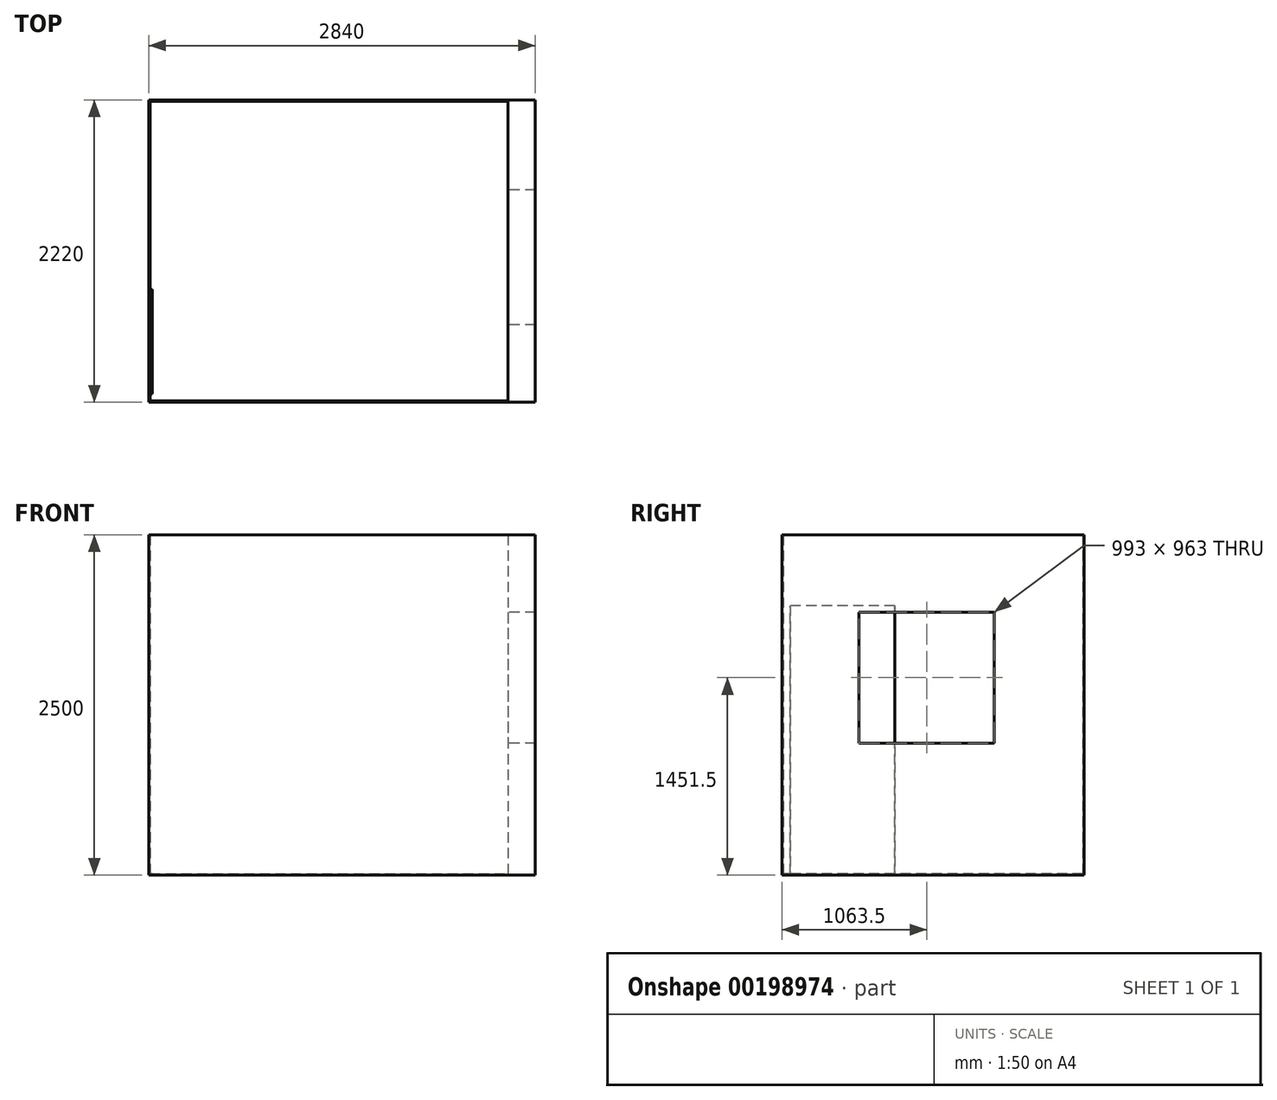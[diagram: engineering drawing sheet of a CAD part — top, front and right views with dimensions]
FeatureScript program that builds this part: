
annotation { "Feature Type Name" : "Feature", "Feature Type Description" : "" }
export const myFeature = defineFeature(function(context is Context, id is Id, definition is map)
    precondition{}
    {
        {
            var Q0;
            Q0=qCreatedBy(makeId("Top.planeOp"),FACE);
            var sketch = newSketch(context, id + "F0", { "sketchPlane" : qUnion([Q0])});
            skLineSegment(sketch, "E0.bottom", {"start": v(-2487.76, 778.4) * mm, "end": v(352.24, 778.4) * mm});
            skLineSegment(sketch, "E0.top", {"start": v(-2487.76, -1441.6) * mm, "end": v(352.24, -1441.6) * mm});
            skLineSegment(sketch, "E0.left", {"start": v(-2487.76, 778.4) * mm, "end": v(-2487.76, -1441.6) * mm});
            skLineSegment(sketch, "E0.right", {"start": v(352.24, 778.4) * mm, "end": v(352.24, -1441.6) * mm});
            skSolve(sketch);
        }
        {
            var Q0;
            Q0=makeQuery(id+"F0.imprint","IMPRINT",FACE,{"disambiguationData":[TD([[makeQuery(id+"F0.imprint","IMPRINT",EDGE,{"derivedFrom":sQuery(id+"F0.wireOp",EDGE,"E0.bottom")}),-1.0]])]});
            extrude(context, id + "F1", {"entities" : qUnion([Q0]), "depth" : 2500 * mm});
        }
        {
            var Q0;
            Q0=makeQuery(id+"F1.opExtrude","CAP_FACE",FACE,{"disambiguationData":[OSD([sQuery(id+"F0.wireOp",EDGE,"E0.bottom"),sQuery(id+"F0.wireOp",EDGE,"E0.top"),sQuery(id+"F0.wireOp",EDGE,"E0.left"),sQuery(id+"F0.wireOp",EDGE,"E0.right")])],"isStart":false});
            shell(context, id + "F2", {"entities" : qUnion([Q0]), "thickness" : 10 * mm});
        }
        {
            var Q0;
            Q0=makeQuery(id+"F2.opShell","OFFSET_FACE",FACE,{"disambiguationData":[OSD([sQuery(id+"F0.wireOp",EDGE,"E0.right")])]});
            extrude(context, id + "F3", {"entities" : qUnion([Q0]), "operationType" : NewBodyOperationType.ADD, "depth" : 190 * mm});
        }
        {
            var Q0;
            Q0=makeQuery(id+"F1.opExtrude","SWEPT_FACE",FACE,{"disambiguationData":[OSD([sQuery(id+"F0.wireOp",EDGE,"E0.left")])]});
            var sketch = newSketch(context, id + "F4", { "sketchPlane" : qUnion([Q0])});
            skLineSegment(sketch, "E1.0", {"start": v(-778.4, 0) * mm, "end": v(1441.6, 0) * mm});
            skLineSegment(sketch, "E1.1", {"start": v(1441.6, 2500) * mm, "end": v(1441.6, 0) * mm});
            skLineSegment(sketch, "E2.bottom", {"start": v(613.6, 1980) * mm, "end": v(1381.6, 1980) * mm});
            skLineSegment(sketch, "E2.top", {"start": v(613.6, 0) * mm, "end": v(1381.6, 0) * mm});
            skLineSegment(sketch, "E2.left", {"start": v(613.6, 1980) * mm, "end": v(613.6, 0) * mm});
            skLineSegment(sketch, "E2.right", {"start": v(1381.6, 1980) * mm, "end": v(1381.6, 0) * mm});
            skLineSegment(sketch, "E3.0.1", {"start": v(1431.6, 2500) * mm, "end": v(1431.6, 10) * mm});
            skLineSegment(sketch, "E3.0.3", {"start": v(1431.6, 10) * mm, "end": v(1431.6, 2500) * mm});
            skSolve(sketch);
        }
        {
            var Q0;
            Q0=makeQuery(id+"F4.imprint","IMPRINT",FACE,{"disambiguationData":[TD([[makeQuery(id+"F4.imprint","IMPRINT",EDGE,{"derivedFrom":sQuery(id+"F4.wireOp",EDGE,"E2.bottom")}),-1.0]])]});
            extrude(context, id + "F5", {"entities" : qUnion([Q0]), "operationType" : NewBodyOperationType.REMOVE, "oppositeDirection" : true, "depth" : 25 * mm});
        }
        {
            var Q0;
            Q0=makeQuery(id+"F3.opExtrude","CAP_FACE",FACE,{"disambiguationData":[OSD([sQuery(id+"F0.wireOp",EDGE,"E0.right")])],"isStart":false});
            var sketch = newSketch(context, id + "F6", { "sketchPlane" : qUnion([Q0])});
            skLineSegment(sketch, "E4.bottom", {"start": v(-118.4, 1933) * mm, "end": v(874.6, 1933) * mm});
            skLineSegment(sketch, "E4.top", {"start": v(-118.4, 970) * mm, "end": v(874.6, 970) * mm});
            skLineSegment(sketch, "E4.left", {"start": v(-118.4, 1933) * mm, "end": v(-118.4, 970) * mm});
            skLineSegment(sketch, "E4.right", {"start": v(874.6, 1933) * mm, "end": v(874.6, 970) * mm});
            skSolve(sketch);
        }
        {
            var Q0;
            Q0=makeQuery(id+"F6.imprint","IMPRINT",FACE,{"disambiguationData":[TD([[makeQuery(id+"F6.imprint","IMPRINT",EDGE,{"derivedFrom":sQuery(id+"F6.wireOp",EDGE,"E4.bottom")}),-1.0]])]});
            extrude(context, id + "F7", {"entities" : qUnion([Q0]), "operationType" : NewBodyOperationType.REMOVE, "oppositeDirection" : true, "depth" : 220 * mm});
        }
    });
